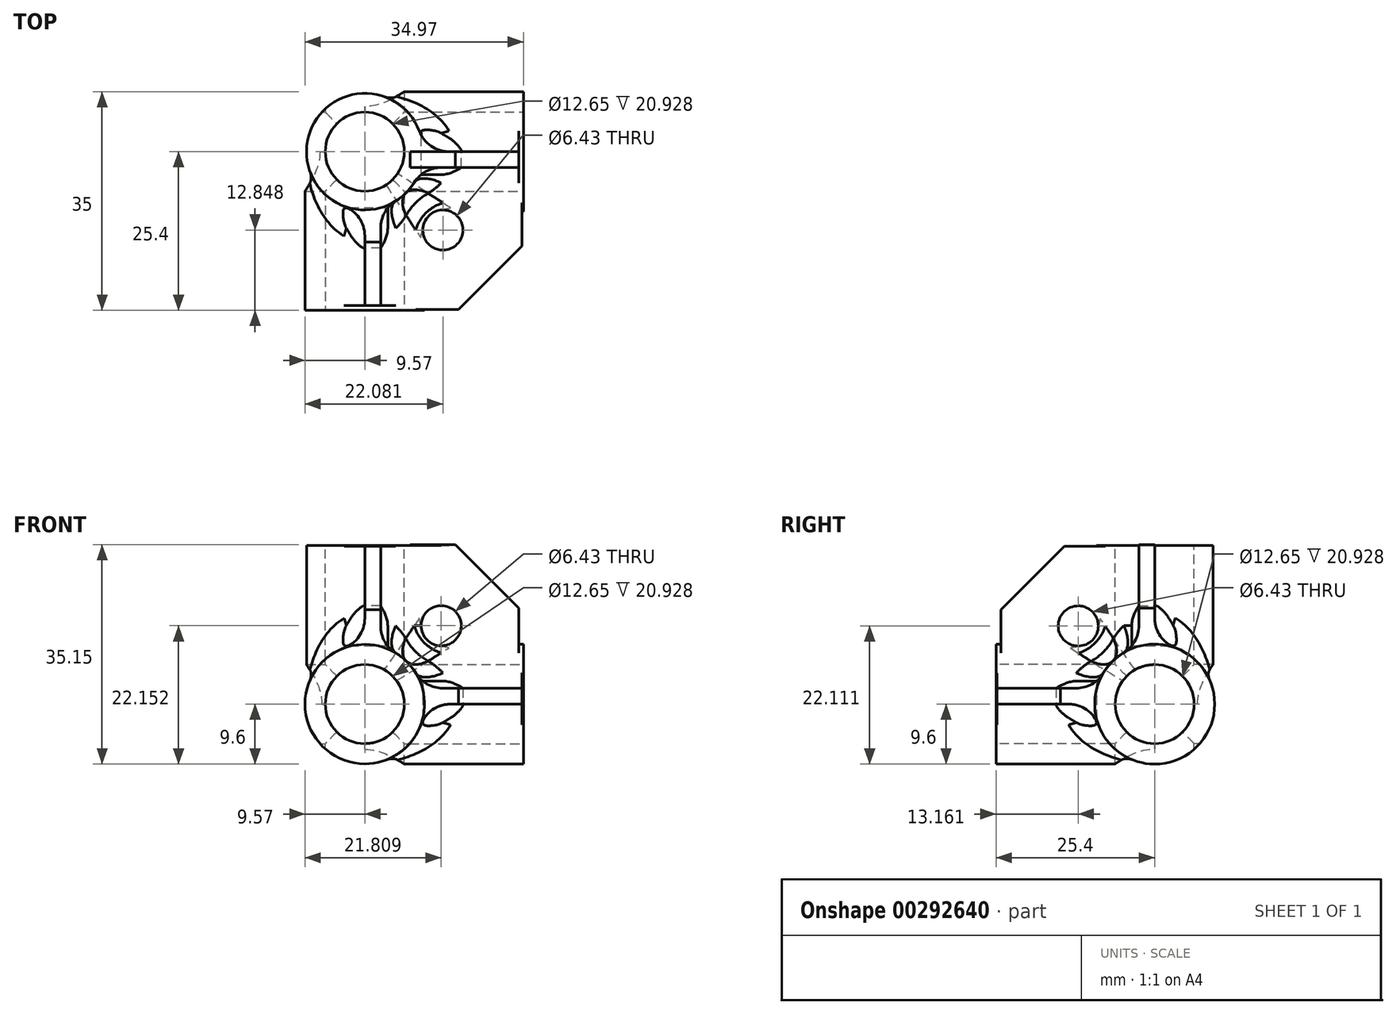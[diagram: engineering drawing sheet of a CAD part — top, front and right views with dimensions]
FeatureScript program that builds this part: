
annotation { "Feature Type Name" : "Feature", "Feature Type Description" : "" }
export const myFeature = defineFeature(function(context is Context, id is Id, definition is map)
    precondition{}
    {
        {
            var Q0;
            Q0=qCreatedBy(makeId("Top.planeOp"),FACE);
            var sketch = newSketch(context, id + "F0", { "sketchPlane" : qUnion([Q0])});
            skCircle(sketch, "E0", {"center": v(0, 0) * mm, "radius": 9.34 * mm});
            skSolve(sketch);
        }
        {
            var Q0;
            Q0=qSketchRegion(id+"F0",true);
            extrude(context, id + "F1", {"entities" : qUnion([Q0]), "depth" : 25.4 * mm});
        }
        {
            var Q0;
            Q0=qCreatedBy(makeId("Right.planeOp"),FACE);
            var sketch = newSketch(context, id + "F2", { "sketchPlane" : qUnion([Q0])});
            skCircle(sketch, "E1", {"center": v(0, 0) * mm, "radius": 9.6 * mm});
            skSolve(sketch);
        }
        {
            var Q0;
            Q0=qSketchRegion(id+"F2",true);
            extrude(context, id + "F3", {"entities" : qUnion([Q0]), "operationType" : NewBodyOperationType.ADD, "depth" : 25.4 * mm});
        }
        {
            var Q0;
            Q0=makeQuery(id+"F3.opExtrude","CAP_FACE",FACE,{"disambiguationData":[OSD([sQuery(id+"F2.wireOp",EDGE,"E1")])],"isStart":false});
            var sketch = newSketch(context, id + "F4", { "sketchPlane" : qUnion([Q0])});
            skPoint(sketch, "E2", {"position": v(0, 0) * mm});
            skSolve(sketch);
        }
        {
            var Q0;
            Q0=makeQuery(id+"F1.opExtrude","CAP_FACE",FACE,{"disambiguationData":[OSD([sQuery(id+"F0.wireOp",EDGE,"E0")])],"isStart":false});
            var sketch = newSketch(context, id + "F5", { "sketchPlane" : qUnion([Q0])});
            skPoint(sketch, "E3", {"position": v(0, 0) * mm});
            skSolve(sketch);
        }
        {
            var Q0;
            Q0=qCreatedBy(makeId("Front.planeOp"),FACE);
            var sketch = newSketch(context, id + "F6", { "sketchPlane" : qUnion([Q0])});
            skLineSegment(sketch, "E4.bottom", {"start": v(7.26, 25.55) * mm, "end": v(24.64, 25.55) * mm});
            skLineSegment(sketch, "E4.top", {"start": v(7.26, 8.17) * mm, "end": v(24.64, 8.17) * mm});
            skLineSegment(sketch, "E4.left", {"start": v(7.26, 25.55) * mm, "end": v(7.26, 8.17) * mm});
            skLineSegment(sketch, "E4.right", {"start": v(24.64, 25.55) * mm, "end": v(24.64, 8.17) * mm});
            skSolve(sketch);
        }
        {
            var Q0;
            Q0=qSketchRegion(id+"F6",true);
            extrude(context, id + "F7", {"entities" : qUnion([Q0]), "operationType" : NewBodyOperationType.ADD, "depth" : 2.54 * mm});
        }
        {
            var Q0;
            Q0=makeQuery(id+"F7.boolean.opBoolean","INTERSECT",EDGE,{"derivedFrom":[makeQuery(id+"F1.opExtrude","SWEPT_FACE",FACE,{"disambiguationData":[OSD([sQuery(id+"F0.wireOp",EDGE,"E0")])]}),makeQuery(id+"F7.opExtrude","CAP_FACE",FACE,{"disambiguationData":[OSD([sQuery(id+"F6.wireOp",EDGE,"E4.bottom"),sQuery(id+"F6.wireOp",EDGE,"E4.top"),sQuery(id+"F6.wireOp",EDGE,"E4.left"),sQuery(id+"F6.wireOp",EDGE,"E4.right")])],"isStart":false})]});
            fillet(context, id + "F8", {"entities" : qUnion([Q0]), "radius" : 5.08 * mm, "tangentPropagation" : true, "allowEdgeOverflow" : false});
        }
        {
            var Q0;
            Q0=makeQuery(id+"F7.boolean.opBoolean","INTERSECT",EDGE,{"derivedFrom":[makeQuery(id+"F3.opExtrude","SWEPT_FACE",FACE,{"disambiguationData":[OSD([sQuery(id+"F2.wireOp",EDGE,"E1")])]}),makeQuery(id+"F7.opExtrude","CAP_FACE",FACE,{"disambiguationData":[OSD([sQuery(id+"F6.wireOp",EDGE,"E4.bottom"),sQuery(id+"F6.wireOp",EDGE,"E4.top"),sQuery(id+"F6.wireOp",EDGE,"E4.left"),sQuery(id+"F6.wireOp",EDGE,"E4.right")])],"isStart":false})]});
            fillet(context, id + "F9", {"entities" : qUnion([Q0]), "radius" : 5.08 * mm, "tangentPropagation" : true, "allowEdgeOverflow" : false});
        }
        {
            var Q0;
            Q0=makeQuery(id+"F7.boolean.opBoolean","INTERSECT",EDGE,{"derivedFrom":[makeQuery(id+"F3.opExtrude","SWEPT_FACE",FACE,{"disambiguationData":[OSD([sQuery(id+"F2.wireOp",EDGE,"E1")])]}),makeQuery(id+"F7.opExtrude","CAP_FACE",FACE,{"disambiguationData":[OSD([sQuery(id+"F6.wireOp",EDGE,"E4.bottom"),sQuery(id+"F6.wireOp",EDGE,"E4.top"),sQuery(id+"F6.wireOp",EDGE,"E4.left"),sQuery(id+"F6.wireOp",EDGE,"E4.right")])],"isStart":true})]});
            var Q1;
            Q1=makeQuery(id+"F7.boolean.opBoolean","INTERSECT",EDGE,{"derivedFrom":[makeQuery(id+"F1.opExtrude","SWEPT_FACE",FACE,{"disambiguationData":[OSD([sQuery(id+"F0.wireOp",EDGE,"E0")])]}),makeQuery(id+"F7.opExtrude","CAP_FACE",FACE,{"disambiguationData":[OSD([sQuery(id+"F6.wireOp",EDGE,"E4.bottom"),sQuery(id+"F6.wireOp",EDGE,"E4.top"),sQuery(id+"F6.wireOp",EDGE,"E4.left"),sQuery(id+"F6.wireOp",EDGE,"E4.right")])],"isStart":true})]});
            fillet(context, id + "F10", {"entities" : qUnion([Q0, Q1]), "radius" : 5.08 * mm, "tangentPropagation" : true, "allowEdgeOverflow" : false});
        }
        {
            var Q0;
            {var subQ0=makeQuery(id+"F1.opExtrude","SWEPT_FACE",FACE,{"disambiguationData":[OSD([sQuery(id+"F0.wireOp",EDGE,"E0")])]});var subQ1=sQuery(id+"F2.wireOp",EDGE,"E1");var subQ2=makeQuery(id+"F3.opExtrude","SWEPT_FACE",FACE,{"disambiguationData":[OSD([subQ1])]});Q0=makeQuery(id+"F7.boolean.opBoolean","SPLIT",EDGE,{"disambiguationData":[TD([makeQuery(id+"F7.opExtrude","CAP_FACE",FACE,{"disambiguationData":[OSD([sQuery(id+"F6.wireOp",EDGE,"E4.bottom"),sQuery(id+"F6.wireOp",EDGE,"E4.top"),sQuery(id+"F6.wireOp",EDGE,"E4.left"),sQuery(id+"F6.wireOp",EDGE,"E4.right")])],"isStart":true})])],"derivedFrom":makeQuery(id+"F3.boolean.opBoolean","INTERSECT",EDGE,{"derivedFrom":[subQ0,subQ2]})});}
            fillet(context, id + "F11", {"entities" : qUnion([Q0]), "radius" : 5.08 * mm, "tangentPropagation" : true, "allowEdgeOverflow" : false});
        }
        {
            var Q0;
            Q0=makeQuery(id+"Fr2Jtv9OpiDKt9A_1.hole-0.boolean.opBoolean","SPLIT",EDGE,{"disambiguationData":[OD(0.0)],"derivedFrom":makeQuery(id+"F3.boolean.opBoolean","INTERSECT",EDGE,{"derivedFrom":[makeQuery(id+"F1.opExtrude","CAP_FACE",FACE,{"disambiguationData":[OSD([sQuery(id+"F0.wireOp",EDGE,"E0")])],"isStart":true}),makeQuery(id+"F3.opExtrude","CAP_FACE",FACE,{"disambiguationData":[OSD([sQuery(id+"F2.wireOp",EDGE,"E1")])],"isStart":true})]})});
            var Q1;
            Q1=makeQuery(id+"Fr2Jtv9OpiDKt9A_1.hole-0.boolean.opBoolean","SPLIT",EDGE,{"disambiguationData":[OD(1.0)],"derivedFrom":makeQuery(id+"F3.boolean.opBoolean","INTERSECT",EDGE,{"derivedFrom":[makeQuery(id+"F1.opExtrude","CAP_FACE",FACE,{"disambiguationData":[OSD([sQuery(id+"F0.wireOp",EDGE,"E0")])],"isStart":true}),makeQuery(id+"F3.opExtrude","CAP_FACE",FACE,{"disambiguationData":[OSD([sQuery(id+"F2.wireOp",EDGE,"E1")])],"isStart":true})]})});
            fillet(context, id + "F12", {"entities" : qUnion([Q0, Q1]), "radius" : 5.08 * mm, "tangentPropagation" : true, "allowEdgeOverflow" : false});
        }
        {
            var Q0;
            Q0=makeQuery(id+"F7.opExtrude","CAP_FACE",FACE,{"disambiguationData":[OSD([sQuery(id+"F6.wireOp",EDGE,"E4.bottom"),sQuery(id+"F6.wireOp",EDGE,"E4.top"),sQuery(id+"F6.wireOp",EDGE,"E4.left"),sQuery(id+"F6.wireOp",EDGE,"E4.right")])],"isStart":false});
            var sketch = newSketch(context, id + "F13", { "sketchPlane" : qUnion([Q0])});
            skPoint(sketch, "E5", {"position": v(12.24, 12.55) * mm});
            skSolve(sketch);
        }
        {
            var Q0;
            Q0=sQuery(id+"F13.wireOp",VERTEX,"E5");
            var Q1;
            Q1=makeQuery(id+"F1.opExtrude","SWEPT_BODY",BODY,{"disambiguationData":[OSD([sQuery(id+"F0.wireOp",EDGE,"E0")])]});
            hole(context, id + "F14", {"style" : HoleStyle.SIMPLE, "endStyle" : HoleEndStyle.THROUGH, "oppositeDirection" : true, "holeDiameter" : 6.43 * mm, "tappedDepth" : 12.7 * mm, "tapClearance" : 3, "locations" : qUnion([Q0]), "scope" : qUnion([Q1])});
        }
        {
            var Q0;
            Q0=sQuery(id+"F13.wireOp",VERTEX,"E5");
            var Q1;
            Q1=makeQuery(id+"F1.opExtrude","SWEPT_BODY",BODY,{"disambiguationData":[OSD([sQuery(id+"F0.wireOp",EDGE,"E0")])]});
            hole(context, id + "F15", {"style" : HoleStyle.SIMPLE, "endStyle" : HoleEndStyle.THROUGH, "holeDiameter" : 6.43 * mm, "tappedDepth" : 12.7 * mm, "tapClearance" : 3, "locations" : qUnion([Q0]), "scope" : qUnion([Q1])});
        }
        {
            var Q0;
            Q0=makeQuery(id+"F7.opExtrude","SWEPT_EDGE",EDGE,{"disambiguationData":[OSD([sQuery(id+"F6.wireOp",EDGE,"E4.bottom"),sQuery(id+"F6.wireOp",EDGE,"E4.right")])]});
            chamfer(context, id + "F16", {"entities" : qUnion([Q0]), "width" : 10.16 * mm, "tangentPropagation" : true});
        }
        {
            var Q0;
            Q0=qCreatedBy(makeId("Front.planeOp"),FACE);
            var sketch = newSketch(context, id + "F17", { "sketchPlane" : qUnion([Q0])});
            skCircle(sketch, "E6", {"center": v(0, 0) * mm, "radius": 9.57 * mm});
            skSolve(sketch);
        }
        {
            var Q0;
            Q0=makeQuery(id+"F17.imprint","IMPRINT",FACE,{"disambiguationData":[TD([[makeQuery(id+"F17.imprint","IMPRINT",EDGE,{"derivedFrom":sQuery(id+"F17.wireOp",EDGE,"E6")}),1.0]])]});
            extrude(context, id + "F18", {"entities" : qUnion([Q0]), "operationType" : NewBodyOperationType.ADD, "depth" : 25.4 * mm});
        }
        {
            var Q0;
            Q0=makeQuery(id+"F18.opExtrude","CAP_FACE",FACE,{"disambiguationData":[OSD([sQuery(id+"F17.wireOp",EDGE,"E6")])],"isStart":false});
            var sketch = newSketch(context, id + "F19", { "sketchPlane" : qUnion([Q0])});
            skPoint(sketch, "E7", {"position": v(0, 0) * mm});
            skSolve(sketch);
        }
        {
            var Q0;
            Q0=makeQuery(id+"F18.boolean.opBoolean","INTERSECT",EDGE,{"derivedFrom":[makeQuery(id+"F12.opFillet","BLEND_FACE",FACE,{"disambiguationData":[OSD([sQuery(id+"F0.wireOp",EDGE,"E0"),sQuery(id+"F2.wireOp",EDGE,"E1")])]}),makeQuery(id+"F18.opExtrude","CAP_FACE",FACE,{"disambiguationData":[OSD([sQuery(id+"F17.wireOp",EDGE,"E6")])],"isStart":true})]});
            fillet(context, id + "F20", {"entities" : qUnion([Q0]), "radius" : 5.08 * mm, "tangentPropagation" : true, "allowEdgeOverflow" : false});
        }
        {
            var Q0;
            Q0=qCreatedBy(makeId("Right.planeOp"),FACE);
            var sketch = newSketch(context, id + "F21", { "sketchPlane" : qUnion([Q0])});
            skLineSegment(sketch, "E8.bottom", {"start": v(0, 0) * mm, "end": v(-24.64, 0) * mm});
            skLineSegment(sketch, "E8.top", {"start": v(0, 25.29) * mm, "end": v(-24.64, 25.29) * mm});
            skLineSegment(sketch, "E8.left", {"start": v(0, 0) * mm, "end": v(0, 25.29) * mm});
            skLineSegment(sketch, "E8.right", {"start": v(-24.64, 0) * mm, "end": v(-24.64, 25.29) * mm});
            skSolve(sketch);
        }
        {
            var Q0;
            Q0=qSketchRegion(id+"F21",true);
            extrude(context, id + "F22", {"entities" : qUnion([Q0]), "operationType" : NewBodyOperationType.ADD, "depth" : 2.54 * mm});
        }
        {
            var Q0;
            Q0=makeQuery(id+"F22.boolean.opBoolean","INTERSECT",EDGE,{"derivedFrom":[makeQuery(id+"F18.opExtrude","SWEPT_FACE",FACE,{"disambiguationData":[OSD([sQuery(id+"F17.wireOp",EDGE,"E6")])]}),makeQuery(id+"F22.opExtrude","CAP_FACE",FACE,{"disambiguationData":[OSD([sQuery(id+"F21.wireOp",EDGE,"E8.bottom"),sQuery(id+"F21.wireOp",EDGE,"E8.top"),sQuery(id+"F21.wireOp",EDGE,"E8.left"),sQuery(id+"F21.wireOp",EDGE,"E8.right")])],"isStart":false})]});
            var Q1;
            Q1=makeQuery(id+"F22.boolean.opBoolean","INTERSECT",EDGE,{"derivedFrom":[makeQuery(id+"F1.opExtrude","SWEPT_FACE",FACE,{"disambiguationData":[OSD([sQuery(id+"F0.wireOp",EDGE,"E0")])]}),makeQuery(id+"F22.opExtrude","CAP_FACE",FACE,{"disambiguationData":[OSD([sQuery(id+"F21.wireOp",EDGE,"E8.bottom"),sQuery(id+"F21.wireOp",EDGE,"E8.top"),sQuery(id+"F21.wireOp",EDGE,"E8.left"),sQuery(id+"F21.wireOp",EDGE,"E8.right")])],"isStart":false})]});
            var Q2;
            {var subQ0=sQuery(id+"F0.wireOp",EDGE,"E0");var subQ1=makeQuery(id+"F1.opExtrude","SWEPT_FACE",FACE,{"disambiguationData":[OSD([subQ0])]});var subQ2=makeQuery(id+"F18.opExtrude","SWEPT_FACE",FACE,{"disambiguationData":[OSD([sQuery(id+"F17.wireOp",EDGE,"E6")])]});Q2=makeQuery(id+"F22.boolean.opBoolean","SPLIT",EDGE,{"disambiguationData":[TD([makeQuery(id+"F9.opFillet","BLEND_FACE",FACE,{"disambiguationData":[OSD([subQ0,sQuery(id+"F2.wireOp",EDGE,"E1")])]})])],"derivedFrom":makeQuery(id+"F18.boolean.opBoolean","INTERSECT",EDGE,{"derivedFrom":[subQ1,subQ2]})});}
            fillet(context, id + "F23", {"entities" : qUnion([Q0, Q1, Q2]), "radius" : 5.08 * mm, "tangentPropagation" : true, "allowEdgeOverflow" : false});
        }
        {
            var Q0;
            Q0=makeQuery(id+"F22.opExtrude","SWEPT_EDGE",EDGE,{"disambiguationData":[OSD([sQuery(id+"F21.wireOp",EDGE,"E8.top"),sQuery(id+"F21.wireOp",EDGE,"E8.right")])]});
            chamfer(context, id + "F24", {"entities" : qUnion([Q0]), "width" : 10.16 * mm, "tangentPropagation" : true});
        }
        {
            var Q0;
            Q0=qCreatedBy(makeId("Top.planeOp"),FACE);
            var sketch = newSketch(context, id + "F25", { "sketchPlane" : qUnion([Q0])});
            skLineSegment(sketch, "E9.bottom", {"start": v(3.37, -3.5) * mm, "end": v(25.16, -3.5) * mm});
            skLineSegment(sketch, "E9.top", {"start": v(3.37, -25.29) * mm, "end": v(25.16, -25.29) * mm});
            skLineSegment(sketch, "E9.left", {"start": v(3.37, -3.5) * mm, "end": v(3.37, -25.29) * mm});
            skLineSegment(sketch, "E9.right", {"start": v(25.16, -3.5) * mm, "end": v(25.16, -25.29) * mm});
            skSolve(sketch);
        }
        {
            var Q0;
            Q0=makeQuery(id+"F25.imprint","IMPRINT",FACE,{"disambiguationData":[TD([[makeQuery(id+"F25.imprint","IMPRINT",EDGE,{"derivedFrom":sQuery(id+"F25.wireOp",EDGE,"E9.bottom")}),-1.0]])]});
            extrude(context, id + "F26", {"entities" : qUnion([Q0]), "operationType" : NewBodyOperationType.ADD, "depth" : 2.54 * mm});
        }
        {
            var Q0;
            Q0=makeQuery(id+"F26.boolean.opBoolean","INTERSECT",EDGE,{"derivedFrom":[makeQuery(id+"F18.opExtrude","SWEPT_FACE",FACE,{"disambiguationData":[OSD([sQuery(id+"F17.wireOp",EDGE,"E6")])]}),makeQuery(id+"F26.opExtrude","CAP_FACE",FACE,{"disambiguationData":[OSD([sQuery(id+"F25.wireOp",EDGE,"E9.bottom"),sQuery(id+"F25.wireOp",EDGE,"E9.top"),sQuery(id+"F25.wireOp",EDGE,"E9.left"),sQuery(id+"F25.wireOp",EDGE,"E9.right")])],"isStart":false})]});
            var Q1;
            Q1=makeQuery(id+"F26.boolean.opBoolean","INTERSECT",EDGE,{"derivedFrom":[makeQuery(id+"F23.opFillet","BLEND_FACE",FACE,{"disambiguationData":[OSD([sQuery(id+"F2.wireOp",EDGE,"E1"),sQuery(id+"F17.wireOp",EDGE,"E6")])]}),makeQuery(id+"F26.opExtrude","CAP_FACE",FACE,{"disambiguationData":[OSD([sQuery(id+"F25.wireOp",EDGE,"E9.bottom"),sQuery(id+"F25.wireOp",EDGE,"E9.top"),sQuery(id+"F25.wireOp",EDGE,"E9.left"),sQuery(id+"F25.wireOp",EDGE,"E9.right")])],"isStart":false})]});
            var Q2;
            Q2=makeQuery(id+"F26.boolean.opBoolean","INTERSECT",EDGE,{"derivedFrom":[makeQuery(id+"F3.opExtrude","SWEPT_FACE",FACE,{"disambiguationData":[OSD([sQuery(id+"F2.wireOp",EDGE,"E1")])]}),makeQuery(id+"F26.opExtrude","CAP_FACE",FACE,{"disambiguationData":[OSD([sQuery(id+"F25.wireOp",EDGE,"E9.bottom"),sQuery(id+"F25.wireOp",EDGE,"E9.top"),sQuery(id+"F25.wireOp",EDGE,"E9.left"),sQuery(id+"F25.wireOp",EDGE,"E9.right")])],"isStart":false})]});
            fillet(context, id + "F27", {"entities" : qUnion([Q0, Q1, Q2]), "radius" : 5.08 * mm, "tangentPropagation" : true, "allowEdgeOverflow" : false});
        }
        {
            var Q0;
            Q0=makeQuery(id+"F26.opExtrude","SWEPT_EDGE",EDGE,{"disambiguationData":[OSD([sQuery(id+"F25.wireOp",EDGE,"E9.top"),sQuery(id+"F25.wireOp",EDGE,"E9.right")])]});
            chamfer(context, id + "F28", {"entities" : qUnion([Q0]), "width" : 10.16 * mm, "tangentPropagation" : true});
        }
        {
            var Q0;
            Q0=makeQuery(id+"F26.boolean.opBoolean","INTERSECT",EDGE,{"derivedFrom":[makeQuery(id+"F18.opExtrude","SWEPT_FACE",FACE,{"disambiguationData":[OSD([sQuery(id+"F17.wireOp",EDGE,"E6")])]}),makeQuery(id+"F26.opExtrude","CAP_FACE",FACE,{"disambiguationData":[OSD([sQuery(id+"F25.wireOp",EDGE,"E9.bottom"),sQuery(id+"F25.wireOp",EDGE,"E9.top"),sQuery(id+"F25.wireOp",EDGE,"E9.left"),sQuery(id+"F25.wireOp",EDGE,"E9.right")])],"isStart":true})]});
            var Q1;
            Q1=makeQuery(id+"F26.boolean.opBoolean","INTERSECT",EDGE,{"derivedFrom":[makeQuery(id+"F23.opFillet","BLEND_FACE",FACE,{"disambiguationData":[OSD([sQuery(id+"F2.wireOp",EDGE,"E1"),sQuery(id+"F17.wireOp",EDGE,"E6")])]}),makeQuery(id+"F26.opExtrude","CAP_FACE",FACE,{"disambiguationData":[OSD([sQuery(id+"F25.wireOp",EDGE,"E9.bottom"),sQuery(id+"F25.wireOp",EDGE,"E9.top"),sQuery(id+"F25.wireOp",EDGE,"E9.left"),sQuery(id+"F25.wireOp",EDGE,"E9.right")])],"isStart":true})]});
            var Q2;
            Q2=makeQuery(id+"F26.boolean.opBoolean","INTERSECT",EDGE,{"derivedFrom":[makeQuery(id+"F3.opExtrude","SWEPT_FACE",FACE,{"disambiguationData":[OSD([sQuery(id+"F2.wireOp",EDGE,"E1")])]}),makeQuery(id+"F26.opExtrude","CAP_FACE",FACE,{"disambiguationData":[OSD([sQuery(id+"F25.wireOp",EDGE,"E9.bottom"),sQuery(id+"F25.wireOp",EDGE,"E9.top"),sQuery(id+"F25.wireOp",EDGE,"E9.left"),sQuery(id+"F25.wireOp",EDGE,"E9.right")])],"isStart":true})]});
            fillet(context, id + "F29", {"entities" : qUnion([Q0, Q1, Q2]), "radius" : 5.08 * mm, "tangentPropagation" : true, "allowEdgeOverflow" : false});
        }
        {
            var Q0;
            {var subQ0=makeQuery(id+"F1.opExtrude","SWEPT_FACE",FACE,{"disambiguationData":[OSD([sQuery(id+"F0.wireOp",EDGE,"E0")])]});var subQ1=sQuery(id+"F17.wireOp",EDGE,"E6");var subQ2=makeQuery(id+"F18.opExtrude","SWEPT_FACE",FACE,{"disambiguationData":[OSD([subQ1])]});Q0=makeQuery(id+"F22.boolean.opBoolean","SPLIT",EDGE,{"disambiguationData":[TD([makeQuery(id+"F18.opExtrude","CAP_FACE",FACE,{"disambiguationData":[OSD([subQ1])],"isStart":true})])],"derivedFrom":makeQuery(id+"F18.boolean.opBoolean","INTERSECT",EDGE,{"derivedFrom":[subQ0,subQ2]})});}
            var Q1;
            Q1=makeQuery(id+"F22.boolean.opBoolean","INTERSECT",EDGE,{"derivedFrom":[makeQuery(id+"F18.opExtrude","SWEPT_FACE",FACE,{"disambiguationData":[OSD([sQuery(id+"F17.wireOp",EDGE,"E6")])]}),makeQuery(id+"F22.opExtrude","CAP_FACE",FACE,{"disambiguationData":[OSD([sQuery(id+"F21.wireOp",EDGE,"E8.bottom"),sQuery(id+"F21.wireOp",EDGE,"E8.top"),sQuery(id+"F21.wireOp",EDGE,"E8.left"),sQuery(id+"F21.wireOp",EDGE,"E8.right")])],"isStart":true})]});
            var Q2;
            Q2=makeQuery(id+"F22.boolean.opBoolean","INTERSECT",EDGE,{"derivedFrom":[makeQuery(id+"F1.opExtrude","SWEPT_FACE",FACE,{"disambiguationData":[OSD([sQuery(id+"F0.wireOp",EDGE,"E0")])]}),makeQuery(id+"F22.opExtrude","CAP_FACE",FACE,{"disambiguationData":[OSD([sQuery(id+"F21.wireOp",EDGE,"E8.bottom"),sQuery(id+"F21.wireOp",EDGE,"E8.top"),sQuery(id+"F21.wireOp",EDGE,"E8.left"),sQuery(id+"F21.wireOp",EDGE,"E8.right")])],"isStart":true})]});
            fillet(context, id + "F30", {"entities" : qUnion([Q0, Q1, Q2]), "radius" : 5.08 * mm, "tangentPropagation" : true, "allowEdgeOverflow" : false});
        }
        {
            var Q0;
            Q0=sQuery(id+"F4.wireOp",VERTEX,"E2");
            var Q1;
            Q1=sQuery(id+"F19.wireOp",VERTEX,"E7");
            var Q2;
            Q2=sQuery(id+"F5.wireOp",VERTEX,"E3");
            var Q3;
            Q3=makeQuery(id+"F1.opExtrude","SWEPT_BODY",BODY,{"disambiguationData":[OSD([sQuery(id+"F0.wireOp",EDGE,"E0")])]});
            hole(context, id + "F31", {"style" : HoleStyle.SIMPLE, "endStyle" : HoleEndStyle.THROUGH, "holeDiameter" : 12.65 * mm, "tappedDepth" : 12.7 * mm, "tapClearance" : 3, "locations" : qUnion([Q0, Q1, Q2]), "scope" : qUnion([Q3])});
        }
        {
            var Q0;
            Q0=makeQuery(id+"F22.opExtrude","CAP_FACE",FACE,{"disambiguationData":[OSD([sQuery(id+"F21.wireOp",EDGE,"E8.bottom"),sQuery(id+"F21.wireOp",EDGE,"E8.top"),sQuery(id+"F21.wireOp",EDGE,"E8.left"),sQuery(id+"F21.wireOp",EDGE,"E8.right")])],"isStart":false});
            var sketch = newSketch(context, id + "F32", { "sketchPlane" : qUnion([Q0])});
            skPoint(sketch, "E10", {"position": v(-12.24, 12.51) * mm});
            skSolve(sketch);
        }
        {
            var Q0;
            Q0=sQuery(id+"F32.wireOp",VERTEX,"E10");
            var Q1;
            Q1=makeQuery(id+"F1.opExtrude","SWEPT_BODY",BODY,{"disambiguationData":[OSD([sQuery(id+"F0.wireOp",EDGE,"E0")])]});
            hole(context, id + "F33", {"style" : HoleStyle.SIMPLE, "endStyle" : HoleEndStyle.THROUGH, "oppositeDirection" : true, "holeDiameter" : 6.43 * mm, "tappedDepth" : 12.7 * mm, "tapClearance" : 3, "locations" : qUnion([Q0]), "scope" : qUnion([Q1])});
        }
        {
            var Q0;
            Q0=sQuery(id+"F32.wireOp",VERTEX,"E10");
            var Q1;
            Q1=makeQuery(id+"F1.opExtrude","SWEPT_BODY",BODY,{"disambiguationData":[OSD([sQuery(id+"F0.wireOp",EDGE,"E0")])]});
            hole(context, id + "F34", {"style" : HoleStyle.SIMPLE, "endStyle" : HoleEndStyle.THROUGH, "holeDiameter" : 6.43 * mm, "tappedDepth" : 12.7 * mm, "tapClearance" : 3, "locations" : qUnion([Q0]), "scope" : qUnion([Q1])});
        }
        {
            var Q0;
            Q0=makeQuery(id+"F26.opExtrude","CAP_FACE",FACE,{"disambiguationData":[OSD([sQuery(id+"F25.wireOp",EDGE,"E9.bottom"),sQuery(id+"F25.wireOp",EDGE,"E9.top"),sQuery(id+"F25.wireOp",EDGE,"E9.left"),sQuery(id+"F25.wireOp",EDGE,"E9.right")])],"isStart":false});
            var sketch = newSketch(context, id + "F35", { "sketchPlane" : qUnion([Q0])});
            skPoint(sketch, "E11", {"position": v(12.51, -12.55) * mm});
            skSolve(sketch);
        }
        {
            var Q0;
            Q0=sQuery(id+"F35.wireOp",VERTEX,"E11");
            var Q1;
            Q1=makeQuery(id+"F1.opExtrude","SWEPT_BODY",BODY,{"disambiguationData":[OSD([sQuery(id+"F0.wireOp",EDGE,"E0")])]});
            hole(context, id + "F36", {"style" : HoleStyle.SIMPLE, "endStyle" : HoleEndStyle.THROUGH, "oppositeDirection" : true, "holeDiameter" : 6.43 * mm, "tappedDepth" : 12.7 * mm, "tapClearance" : 3, "locations" : qUnion([Q0]), "scope" : qUnion([Q1])});
        }
        {
            var Q0;
            Q0=sQuery(id+"F35.wireOp",VERTEX,"E11");
            var Q1;
            Q1=makeQuery(id+"F1.opExtrude","SWEPT_BODY",BODY,{"disambiguationData":[OSD([sQuery(id+"F0.wireOp",EDGE,"E0")])]});
            hole(context, id + "F37", {"style" : HoleStyle.SIMPLE, "endStyle" : HoleEndStyle.THROUGH, "holeDiameter" : 6.43 * mm, "tappedDepth" : 12.7 * mm, "tapClearance" : 3, "locations" : qUnion([Q0]), "scope" : qUnion([Q1])});
        }
    });
